# Revit family: Shower-Shower_Door-KOHLER-Levity-K-706012_1
name_source: partatom
category: Specialty Equipment
revit_build: Autodesk Revit 2017 (Build: 20160225_1515(x64)
units: mm (PartAtom-declared; Revit-internal decimal feet)

## family parameters
Cut with Voids When Loaded = No
Host = Face
OmniClass Number = 23.31.17.17
OmniClass Title = Shower Enclosures
Part Type = Normal
Room Calculation Point = No
Round Connector Dimension = Use Diameter
Shared = No

## types (5) — shared parameters
ADA Compliant = No
Assembly Code = C1030200
Date Modified = 08/17/2020
Default Elevation = 0"
Description = Sliding shower door, 74 inch H x 56-5/8 - 59-5/8 inch W, with 3/8 inch thick Crystal Clear glass
Glass Finish = Kohler-Glass-L-Crystal_Clear
Height = 74"
Length = 2 15/16"
Manufacturer = KOHLER Co.
Master Format 2014 = 10 28 00
Master Format 2014 Name = Toilet, Bath, and Laundry Accessories
Material = Premium Metal Construction
Product Documentation Link = https://www.us.kohler.com
Product Name = Levity
Product Page URL = http://www.us.kohler.com
URL = https://www.us.kohler.com
WaterSense Certified = No

## per-type parameters (varying)
| type | Finish | Model | Type |
| SHP-Bright Polished Silver | Kohler-Metal-SHP-Bright_Polished_Silver | K-706012-L-SHP | 1 |
| ABV-Anodized Brushed Bronze | Kohler-Metal-ABV-Anodized_Brushed_Bronze | K-706012-L-ABV | 3 |
| ABZ-Anodized Dark Bronze | Kohler-Metal-ABZ-Anodized_Dark_Bronze | K-706012-L-ABZ | 4 |
| NX-Brushed Nickel | Kohler-Metal-NX-Brushed_Nickel | K-706012-L-NX | 2 |
| BL-Matte Black | Kohler-Metal-BL-Matte_Black | K-706012-L-BL | 5 |

## geometry (parser evidence)
native form markers: Sweep x4
no freeform markers — native parametric forms only
